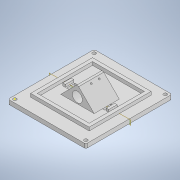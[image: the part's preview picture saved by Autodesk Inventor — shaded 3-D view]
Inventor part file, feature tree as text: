
AUTODESK INVENTOR PART (.ipt)
format: ipt  version: 2022 (Build 260153000, 153)  size: 252,928 bytes
history: native  units: mm
features: extrude x10, sketch x9, other x2, fillet x2
ambient origin geometry x8: Origin, YZ Plane, XZ Plane, XY Plane, X Axis, Y Axis, Z Axis, Center Point
bodies: Body1 (feature_tree)
feature tree (23):
  other  "Těleso1"
  sketch  "Náčrt1"
  extrude  "Vysunutí1"  Depth=4.0mm
  extrude  "Vysunutí2"  Depth=4.0mm
  fillet  "Zaoblení1"  Radius=4.0mm
  sketch  "Náčrt2"
  other  "Pracovní rovina1"
  extrude  "Vysunutí3"  Depth=4.0mm
  fillet  "Zaoblení2"  Radius=85.0mm
  extrude  "Vysunutí4"  Depth=95.0mm
  extrude  "Vysunutí5"  Depth=4.0mm
  sketch  "Náčrt6"
  sketch  "Náčrt7"
  extrude  "Vysunutí6"  Depth=4.0mm
  extrude  "Vysunutí7"  Depth=4.0mm
  sketch  "Náčrt8"
  extrude  "Vysunutí8"  Depth=4.0mm
  extrude  "Vysunutí9"  Depth=4.0mm
  extrude  "Vysunutí10"  Depth=4.0mm
  sketch  "Náčrt3"
  sketch  "Náčrt4"
  sketch  "Náčrt5"
  sketch  "Náčrt9"
